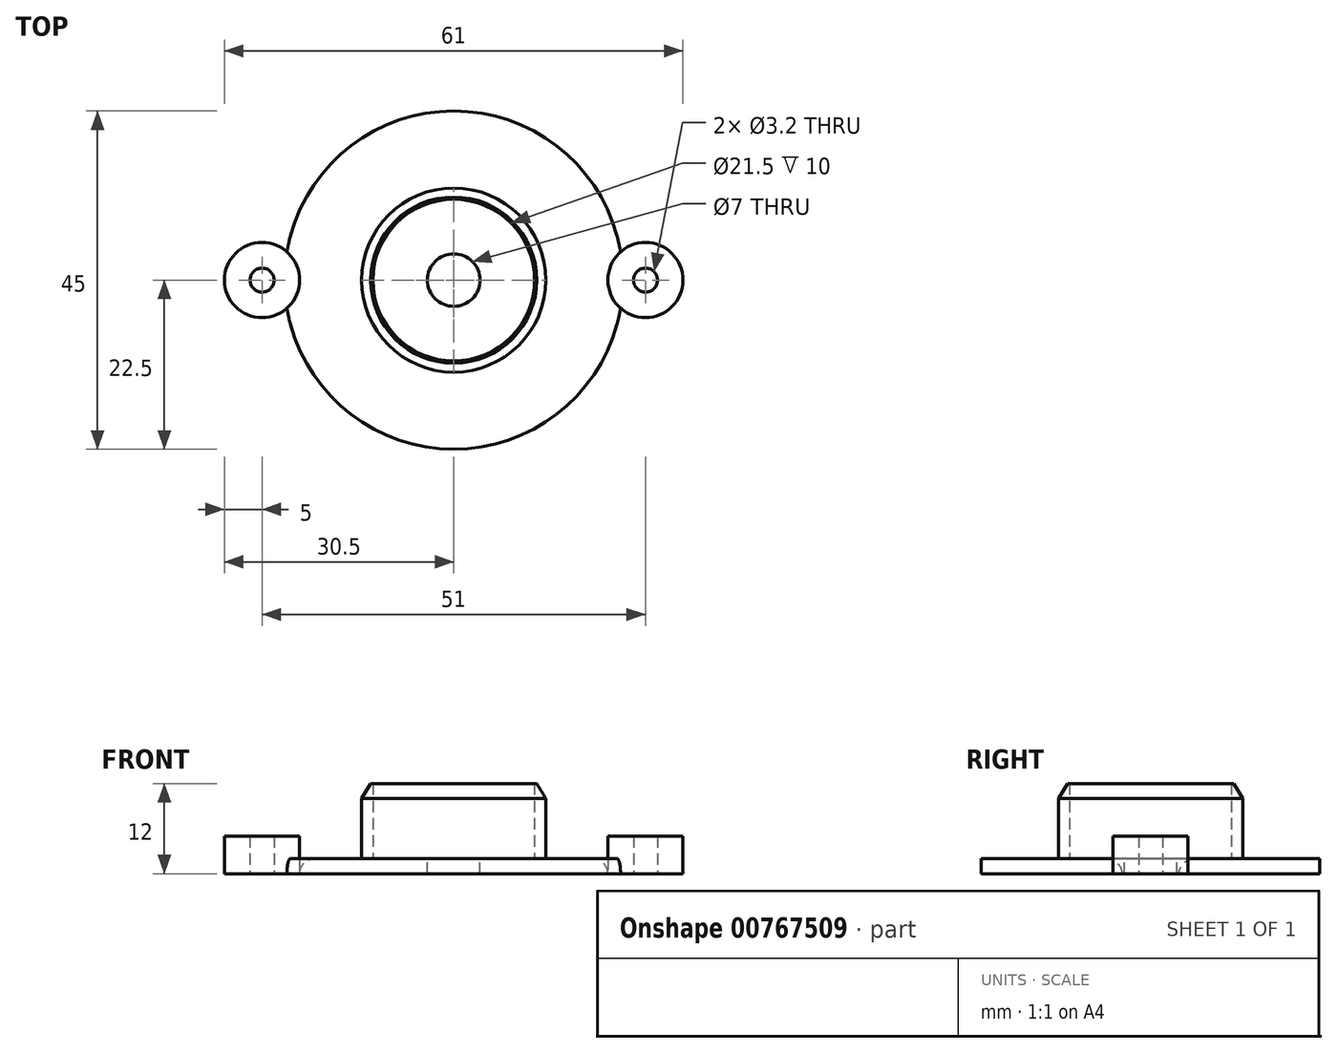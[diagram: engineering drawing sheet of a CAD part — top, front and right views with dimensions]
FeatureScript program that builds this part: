
annotation { "Feature Type Name" : "Feature", "Feature Type Description" : "" }
export const myFeature = defineFeature(function(context is Context, id is Id, definition is map)
    precondition{}
    {
        {
            var Q0;
            Q0=qCreatedBy(makeId("Top.planeOp"),FACE);
            var sketch = newSketch(context, id + "F0", { "sketchPlane" : qUnion([Q0])});
            skCircle(sketch, "E0", {"center": v(0, 0) * mm, "radius": 22.5 * mm});
            skCircle(sketch, "E1", {"center": v(25.5, 0) * mm, "radius": 5 * mm});
            skCircle(sketch, "E2", {"center": v(25.5, 0) * mm, "radius": 1.6 * mm});
            skCircle(sketch, "E3.1.0", {"center": v(-25.5, 0) * mm, "radius": 5 * mm});
            skCircle(sketch, "E3.1.1", {"center": v(-25.5, 0) * mm, "radius": 1.6 * mm});
            skSolve(sketch);
        }
        {
            var Q0;
            Q0=makeQuery(id+"F0.imprint","IMPRINT",FACE,{"disambiguationData":[TD([[makeQuery(id+"F0.imprint","IMPRINT",EDGE,{"derivedFrom":sQuery(id+"F0.wireOp",EDGE,"E3.1.1")}),-1.0]])]});
            var Q1;
            {var subQ0=sQuery(id+"F0.wireOp",EDGE,"E3.1.0");var subQ1=sQuery(id+"F0.wireOp",EDGE,"E0");var subQ2=makeQuery(id+"F0.imprint","INTERSECT",VERTEX,{"disambiguationData":[OD(0.0)],"derivedFrom":[subQ1,subQ0]});Q1=makeQuery(id+"F0.imprint","IMPRINT",FACE,{"disambiguationData":[TD([[makeQuery(id+"F0.imprint","IMPRINT",EDGE,{"disambiguationData":[TD([[subQ2,-1.0]])],"derivedFrom":subQ1}),1.0]])]});}
            var Q2;
            Q2=makeQuery(id+"F0.imprint","IMPRINT",FACE,{"disambiguationData":[TD([[makeQuery(id+"F0.imprint","IMPRINT",EDGE,{"derivedFrom":sQuery(id+"F0.wireOp",EDGE,"E2")}),-1.0]])]});
            var Q3;
            {var subQ0=sQuery(id+"F0.wireOp",EDGE,"E1");var subQ1=sQuery(id+"F0.wireOp",EDGE,"E0");var subQ2=makeQuery(id+"F0.imprint","INTERSECT",VERTEX,{"disambiguationData":[OD(0.0)],"derivedFrom":[subQ1,subQ0]});Q3=makeQuery(id+"F0.imprint","IMPRINT",FACE,{"disambiguationData":[TD([[makeQuery(id+"F0.imprint","IMPRINT",EDGE,{"disambiguationData":[TD([[subQ2,1.0]])],"derivedFrom":subQ1}),1.0]])]});}
            extrude(context, id + "F1", {"entities" : qUnion([Q0, Q1, Q2, Q3]), "depth" : 5 * mm, "offsetDistance" : 25 * mm});
        }
        {
            var Q0;
            {var subQ0=sQuery(id+"F0.wireOp",EDGE,"E3.1.0");var subQ1=sQuery(id+"F0.wireOp",EDGE,"E0");var subQ2=makeQuery(id+"F0.imprint","INTERSECT",VERTEX,{"disambiguationData":[OD(0.0)],"derivedFrom":[subQ1,subQ0]});Q0=makeQuery(id+"F0.imprint","IMPRINT",FACE,{"disambiguationData":[TD([[makeQuery(id+"F0.imprint","IMPRINT",EDGE,{"disambiguationData":[TD([[subQ2,1.0]])],"derivedFrom":subQ1}),1.0]])]});}
            extrude(context, id + "F2", {"entities" : qUnion([Q0]), "depth" : 2 * mm, "offsetDistance" : 25 * mm});
        }
        {
            var Q0;
            Q0=makeQuery(id+"F2.opExtrude","CAP_FACE",FACE,{"disambiguationData":[OSD([sQuery(id+"F0.wireOp",EDGE,"E0"),sQuery(id+"F0.wireOp",EDGE,"E1"),sQuery(id+"F0.wireOp",EDGE,"E3.1.0")])],"isStart":false});
            var sketch = newSketch(context, id + "F3", { "sketchPlane" : qUnion([Q0])});
            skCircle(sketch, "E4", {"center": v(0, 0) * mm, "radius": 10.75 * mm});
            skCircle(sketch, "E5", {"center": v(0, 0) * mm, "radius": 12.25 * mm});
            skSolve(sketch);
        }
        {
            var Q0;
            Q0=makeQuery(id+"F3.imprint","IMPRINT",FACE,{"disambiguationData":[TD([[makeQuery(id+"F3.imprint","IMPRINT",EDGE,{"derivedFrom":sQuery(id+"F3.wireOp",EDGE,"E4")}),-1.0]])]});
            var Q1;
            {var subQ1=makeQuery(id+"F2.opExtrude","CAP_EDGE",EDGE,{"disambiguationData":[OSD([sQuery(id+"F0.wireOp",EDGE,"E3.1.0")])],"isStart":false});Q1=makeQuery(id+"F3.imprint","IMPRINT",FACE,{"disambiguationData":[TD([[makeQuery(id+"F3.imprint","IMPRINT",EDGE,{"derivedFrom":subQ1}),1.0]])]});}
            var Q2;
            {var subQ1=makeQuery(id+"F2.opExtrude","CAP_EDGE",EDGE,{"disambiguationData":[OSD([sQuery(id+"F0.wireOp",EDGE,"E1")])],"isStart":false});Q2=makeQuery(id+"F3.imprint","IMPRINT",FACE,{"disambiguationData":[TD([[makeQuery(id+"F3.imprint","IMPRINT",EDGE,{"derivedFrom":subQ1}),1.0]])]});}
            extrude(context, id + "F4", {"entities" : qUnion([Q0, Q1, Q2]), "depth" : 10 * mm, "offsetDistance" : 25 * mm});
        }
        {
            var Q0;
            Q0=makeQuery(id+"F4.opExtrude","CAP_EDGE",EDGE,{"disambiguationData":[OSD([sQuery(id+"F3.wireOp",EDGE,"E5")])],"isStart":false});
            chamfer(context, id + "F5", {"entities" : qUnion([Q0]), "chamferType" : ChamferType.TWO_OFFSETS, "width1" : 1.2 * mm, "oppositeDirection" : false, "width2" : 2 * mm, "tangentPropagation" : true});
        }
        {
            var Q0;
            Q0=makeQuery(id+"FuXeZ9usWzECoiR_2.boolean.opBoolean","SPLIT",FACE,{"disambiguationData":[TD([makeQuery(id+"FuXeZ9usWzECoiR_2.opExtrude","SWEPT_FACE",FACE,{"disambiguationData":[OSD([sQuery(id+"F3.wireOp",EDGE,"E4")])]})])],"derivedFrom":makeQuery(id+"F2.opExtrude","CAP_FACE",FACE,{"disambiguationData":[OSD([sQuery(id+"F0.wireOp",EDGE,"E0"),sQuery(id+"F0.wireOp",EDGE,"E1"),sQuery(id+"F0.wireOp",EDGE,"E3.1.0")])],"isStart":false})});
            var sketch = newSketch(context, id + "F6", { "sketchPlane" : qUnion([Q0])});
            skCircle(sketch, "E6", {"center": v(0, 0) * mm, "radius": 3.5 * mm});
            skSolve(sketch);
        }
        {
            var Q0;
            Q0=makeQuery(id+"F6.imprint","IMPRINT",FACE,{"disambiguationData":[TD([[makeQuery(id+"F6.imprint","IMPRINT",EDGE,{"derivedFrom":sQuery(id+"F6.wireOp",EDGE,"E6")}),1.0]])]});
            extrude(context, id + "F7", {"entities" : qUnion([Q0]), "operationType" : NewBodyOperationType.REMOVE, "oppositeDirection" : true, "depth" : 2 * mm, "offsetDistance" : 25 * mm});
        }
        {
            var Q0;
            Q0=makeQuery(id+"F2.opExtrude","CAP_EDGE",EDGE,{"disambiguationData":[OSD([sQuery(id+"F0.wireOp",EDGE,"E3.1.0")])],"isStart":false});
            var Q1;
            Q1=makeQuery(id+"F2.opExtrude","CAP_EDGE",EDGE,{"disambiguationData":[OSD([sQuery(id+"F0.wireOp",EDGE,"E1")])],"isStart":false});
            fillet(context, id + "F8", {"entities" : qUnion([Q0, Q1]), "radius" : 2 * mm, "tangentPropagation" : true, "allowEdgeOverflow" : false});
        }
    });
